# Revit family: Sliding_Glass-By_Pass-PGT-Aluminum_Premium-SGD780-XXd
name_source: partatom
category: Doors
revit_build: Autodesk Revit 2015 (Build: 20160512_1515(x64)
units: mm (PartAtom-declared; Revit-internal decimal feet)

## types (1)
- Refer to Type Catalog
    Analytic Construction = <None>
    Assembly Code = B2030110
    Color Glass = Glass - PGT - Clear
    Custom Design Note = The types included show default grid/size configurations.  Please reference the 'Product Style Guide' to see all standard configurations and restrictions before creating custom designs.  Please contact PGT Industries with any questions regarding custom designs.
    Description = Aluminum Premium Sliding Glass Door
    Door Panel Height = 120"
    Door Panel Width = 60"
    Finish = Metal - PGT - Paint - White
    Flush Riser = Yes
    Function = Exterior
    Glass Thickness = 1"
    Grid = Yes
    Grid Layout Note = To edit the grid layout ensure the 'Grid' parameter is turned on and then select an option from the 'Grid Type' drop down.  Please refer to the 'Product Style Guide' for standard configurations and restrictions.
    Grid Type = Face_Based_Mullion_ Glass : BP9
    Hardware Height = 36"
    Hardware Material = Steel AISI 4620
    Height = 122 3/16"
    High Riser = No
    Low Riser = No
    Manufacturer = PGT Industries
    Maximum Panel Size = 5' x 10' OR 4' x 12'
    Medium Riser = No
    Minimum Panel Size = 28” x 32 5/8”
    Model = SGD780 2P2T XX
    Offset From Wall Center = 0"
    Optional 9-Inch Bottom Rail = No
    Panel Offset = 6 1/16"
    Plan View Offset = 38 29/32"
    Product Page URL = http://www.pgtindustries.com
    Product Style Guide = http://www.pgtindustries.com
    Rough Height = 122 3/16"
    Rough Width = 116 11/16"
    Standard Riser = No
    Type Comments = Double Door
    URL = http://www.pgtindustries.com
    Wall Closure = By host
    Width = 116 11/16"

## geometry (parser evidence)
native form markers: Sweep x28
no freeform markers — native parametric forms only
